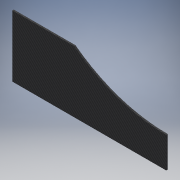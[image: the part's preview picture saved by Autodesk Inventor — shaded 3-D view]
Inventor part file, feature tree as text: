
AUTODESK INVENTOR PART (.ipt)
format: ipt  version: 2018 (Build 220112000, 112)  size: 118,784 bytes
history: native  units: mm
features: sketch x3, extrude x2, other x1
ambient origin geometry x8: Origin, YZ Plane, XZ Plane, XY Plane, X Axis, Y Axis, Z Axis, Center Point
bodies: Body1 (feature_tree)
feature tree (6):
  other  "ソリッド1"
  extrude  "押し出し1"  Depth=500.0mm
  extrude  "押し出し3"  Depth=200.0mm
  sketch  "スケッチ4"
  sketch  "スケッチ1"
  sketch  "スケッチ3"
